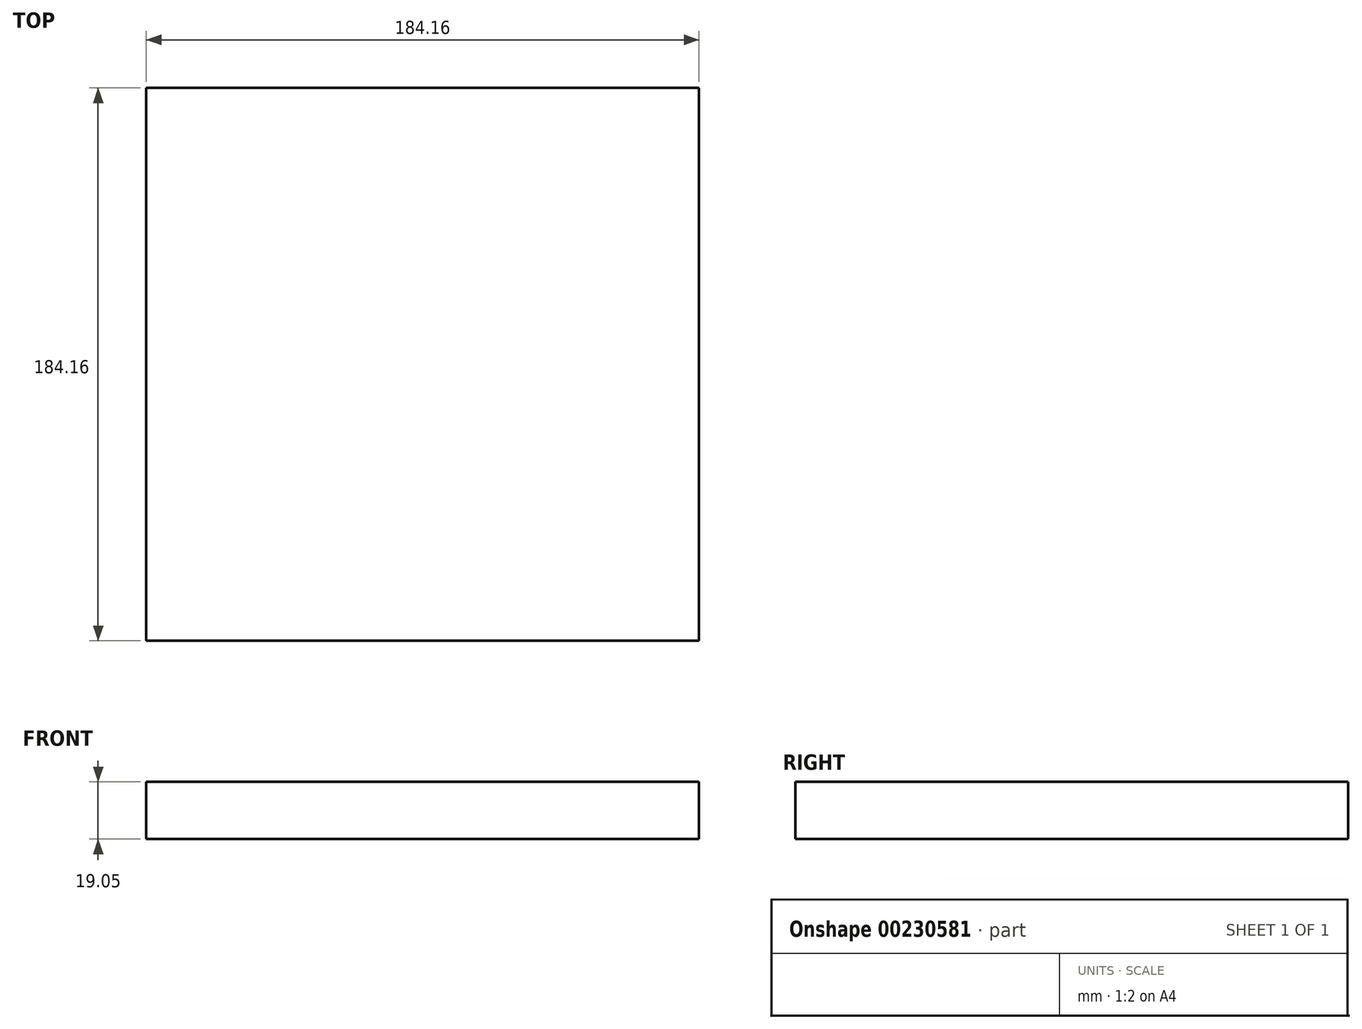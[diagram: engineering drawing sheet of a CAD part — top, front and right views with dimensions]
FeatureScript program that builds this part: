
annotation { "Feature Type Name" : "Feature", "Feature Type Description" : "" }
export const myFeature = defineFeature(function(context is Context, id is Id, definition is map)
    precondition{}
    {
        {
            var Q0;
            Q0=qCreatedBy(makeId("Top.planeOp"),FACE);
            var sketch = newSketch(context, id + "F0", { "sketchPlane" : qUnion([Q0])});
            skLineSegment(sketch, "E0.bottom", {"start": v(-92.07, -92.08) * mm, "end": v(92.08, -92.08) * mm});
            skLineSegment(sketch, "E0.top", {"start": v(-92.08, 92.07) * mm, "end": v(92.07, 92.07) * mm});
            skLineSegment(sketch, "E0.left", {"start": v(-92.08, -92.08) * mm, "end": v(-92.08, 92.07) * mm});
            skLineSegment(sketch, "E0.right", {"start": v(92.08, -92.08) * mm, "end": v(92.07, 92.07) * mm});
            skPoint(sketch, "E0.middle", {"position": v(0, 0) * mm});
            skSolve(sketch);
        }
        {
            var Q0;
            Q0 = qSketchRegion(id + "F0", true);
            extrude(context, id + "F1", {"entities" : qUnion([Q0]), "depth" : 19.05 * mm});
        }
    });
